# Revit family: NAU_Naughtone_Tbls_AliTables_Updated_18.02.2019_
name_source: partatom
category: Furniture
revit_build: Autodesk Revit 2016 (Build: 20150220_1215(x64)
units: mm (PartAtom-declared; Revit-internal decimal feet)

## family parameters
Always vertical = Yes
Cut with Voids When Loaded = No
OmniClass Number = 23.40.20.00
OmniClass Title = General Furniture and Specialties
Room Calculation Point = No
Shared = Yes
Work Plane-Based = No

## types (11) — shared parameters
Assembly Code = E2020200
AssetType = Movable
BIMObjectName = NAU_Naughtone_Tables_AliTables
BaseMaterial = NAU_Generic_Metal_White
Category = Pr_40_50_21 : Desks, tables and worktops
DurationUnit = year
ExpectedLife = 5
Finish = Black/white base, also available in 16x RAL colours. white/black laminate top or oak/walnut veneer top
IfcExportAs = IfcFurnishingElementType
IfcExportType = TABLE
Keynote = Pr_40_50_21
ManufacturerAddress = Knaresborough Tech Park, Manse Lane, Knaresborough, HG5 8LF
ManufacturerName = Naughtone
ManufacturerURL = www.naughtone.com
Material = Steel, Aluminium, wood
NBSDescription = Tables
NBSReference = 45-35-86/327
Name = Tables_AliTables_Naughtone
SustainabilityPerformance = FSC certifeied, SCS indoor advantage gold
TopMaterial = NAU_Generic_Wood_Oak
URL = www.naughtone.com
Uniclass2015Code = Pr_40_50_21
Uniclass2015Title = Desks, tables and worktops
Uniclass2015Version = Products v1.10
Version = 1
WarrantyDurationLabor = 5
WarrantyDurationParts = 5
WarrantyDurationUnit = year
zero-valued in all types: NumberOfChairs, WorksurfaceArea

## per-type parameters (varying)
| type | Description | HeightOfLeg | IsAngeldPlate | IsCircularTop | IsLargerBase | IsLargerBaseAngled | IsSmallerBase | IsSmallerBaseAngled | IsSquarePlate | IsSquareTop | Model | ModelNumber | ModelReference | NominalHeight | NominalLength | NominalWidth | Shape | Size |
| Ali 650 dia coffee table ALI650DL 650 dia x 450 mm | Ali 650 dia coffee table | 252 mm  [stored 0.826772 ft] | Yes | Yes | No | No | Yes | No | No | No | ALI650DL | ALI650DL | Ali 650 dia coffee table | 450 mm  [stored 1.47638 ft] | 650 mm  [stored 2.13255 ft] | 650 mm  [stored 2.13255 ft] | Circular | 650⌀ x 450mm |
| Ali 650 square coffee table ALI650SL 650 x 650 x 450 mm | Ali 650 square coffee table | 252 mm  [stored 0.826772 ft] | No | No | No | No | No | Yes | Yes | Yes | ALI650SL | ALI650SL | Ali 650 square coffee table | 450 mm  [stored 1.47638 ft] | 650 mm  [stored 2.13255 ft] | 650 mm  [stored 2.13255 ft] | Square | 650 x 650 x 450 mm |
| Ali 850 dia coffee table ALI850DL 850 dia x 450 mm | Ali 850 dia coffee table | 252 mm  [stored 0.826772 ft] | Yes | Yes | Yes | No | No | No | No | No | ALI850DL | ALI850DL | Ali 850 dia coffee table | 450 mm  [stored 1.47638 ft] | 850 mm  [stored 2.78871 ft] | 850 mm  [stored 2.78871 ft] | Circular | 850⌀ x 450mm |
| Ali 850 square coffee table ALI850SL 850 x 850 x 450 mm | Ali 850 square coffee table | 252 mm  [stored 0.826772 ft] | No | No | No | Yes | No | No | Yes | Yes | ALI850SL | ALI850SL | Ali 850 square coffee table | 450 mm  [stored 1.47638 ft] | 850 mm  [stored 2.78871 ft] | 850 mm  [stored 2.78871 ft] | Square | 850 x 850 x 450 mm |
| Ali 650 dia cafe table ALI650D 650 dia x 750 mm | Ali 650 dia cafe table | 552 mm  [stored 1.81102 ft] | Yes | Yes | No | No | Yes | No | No | No | ALI650D | ALI650D | Ali 650 dia cafe table | 750 mm  [stored 2.46063 ft] | 650 mm  [stored 2.13255 ft] | 650 mm  [stored 2.13255 ft] | Circular | 650⌀ x 750mm |
| Ali 650 square cafe table ALI650S 650 x 650 x 750 mm | Ali 650 square cafe table | 552 mm  [stored 1.81102 ft] | No | No | No | No | No | Yes | Yes | Yes | ALI650S | ALI650S | Ali 650 square cafe table | 750 mm  [stored 2.46063 ft] | 650 mm  [stored 2.13255 ft] | 650 mm  [stored 2.13255 ft] | Square | 650 x 650 x 750mm |
| Ali 850 dia cafe table ALI850D 850 dia x 750 mm | Ali 850 dia cafe table | 552 mm  [stored 1.81102 ft] | Yes | Yes | Yes | No | No | No | No | No | ALI850D | ALI850D | Ali 850 dia cafe table | 750 mm  [stored 2.46063 ft] | 850 mm  [stored 2.78871 ft] | 850 mm  [stored 2.78871 ft] | Circular | 850⌀ x 750mm |
| Ali 850 square cafe table ALI850S 850 x 850 x 750 mm | Ali 850 square cafe table | 552 mm  [stored 1.81102 ft] | No | No | No | Yes | No | No | Yes | Yes | ALI850S | ALI850S | Ali 850 square cafe table | 750 mm  [stored 2.46063 ft] | 850 mm  [stored 2.78871 ft] | 850 mm  [stored 2.78871 ft] | Square | 850 x 850 x 750 mm |
| Ali 650 dia poseur height table ALI650DH 650 dia x 1000 mm | Ali 650 dia poseur height table | 802 mm  [stored 2.63123 ft] | Yes | Yes | No | Yes | No | No | No | No | ALI650DH | ALI650DH | Ali 650 dia poseur height table | 1000 mm  [stored 3.28084 ft] | 650 mm  [stored 2.13255 ft] | 650 mm  [stored 2.13255 ft] | Circular | 650⌀ x 1000mm |
| Ali 650 square poseur height table ALI650SH 650 x 650 x 1000 mm | Ali 650 square poseur height table | 802 mm  [stored 2.63123 ft] | No | No | No | Yes | No | No | Yes | Yes | ALI650SH | ALI650SH | Ali 650 square poseur height table | 1000 mm  [stored 3.28084 ft] | 650 mm  [stored 2.13255 ft] | 650 mm  [stored 2.13255 ft] | Square | 650 x 650 x 1000mm |
| Ali 850 dia poseur height table ALI850DH 850 dia x 1000 mm | Ali 850 dia poseur height table | 802 mm  [stored 2.63123 ft] | Yes | Yes | Yes | No | No | No | No | No | ALI850DH | ALI850DH | Ali 850 dia poseur height table | 1000 mm  [stored 3.28084 ft] | 850 mm  [stored 2.78871 ft] | 850 mm  [stored 2.78871 ft] | Circular | 850⌀ x 1000mm |

note: [stored X ft] marks values corroborated as IEEE doubles in the binary element streams (Revit-internal decimal feet)

## geometry (parser evidence)
native form markers: Sweep x12
no freeform markers — native parametric forms only
